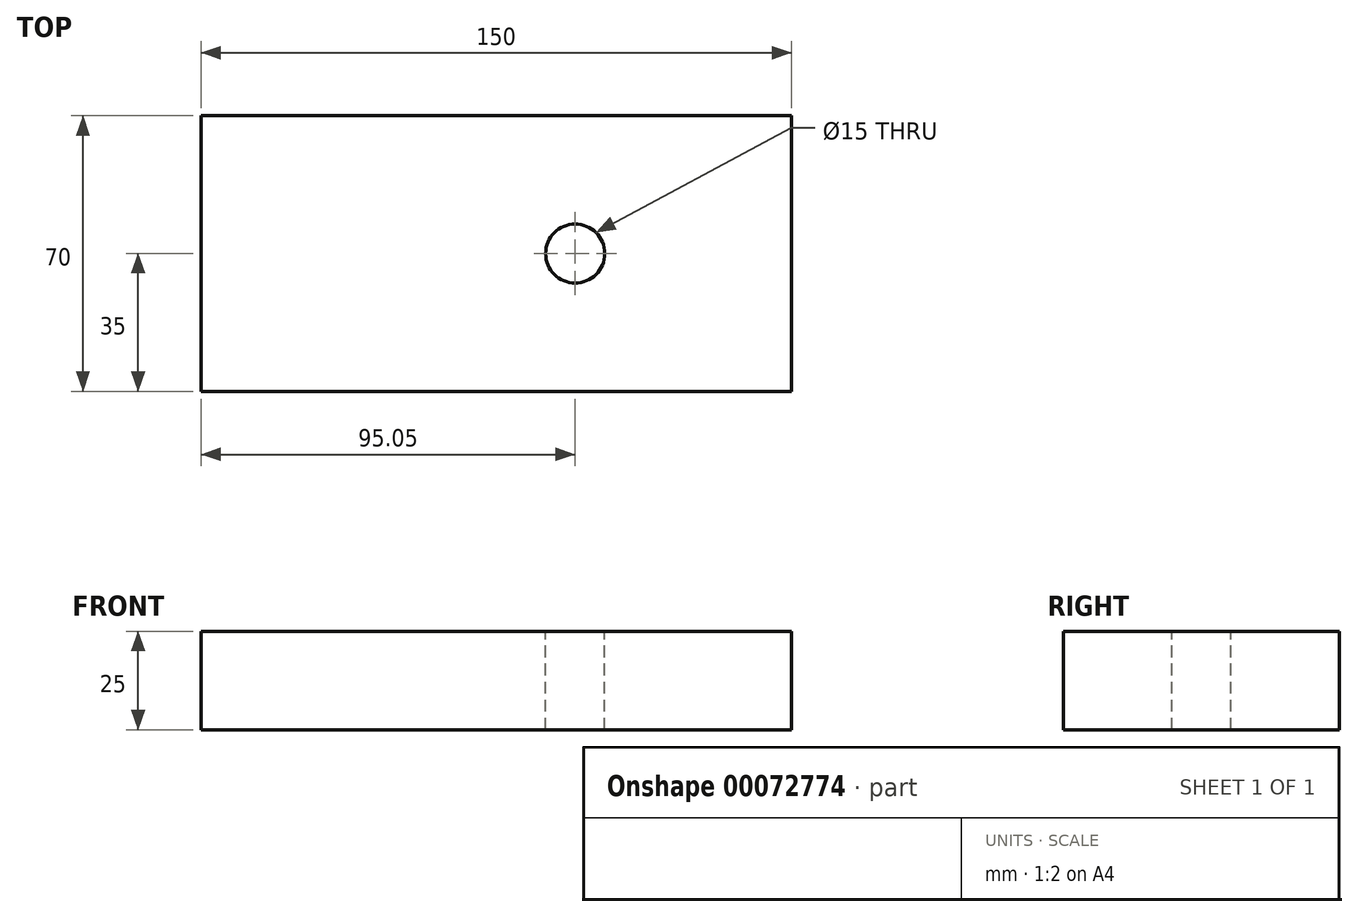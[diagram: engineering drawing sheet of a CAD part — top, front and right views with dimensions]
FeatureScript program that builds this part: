
annotation { "Feature Type Name" : "Feature", "Feature Type Description" : "" }
export const myFeature = defineFeature(function(context is Context, id is Id, definition is map)
    precondition{}
    {
        {
            var Q0;
            Q0=qCreatedBy(makeId("Top.planeOp"),FACE);
            var sketch = newSketch(context, id + "F0", { "sketchPlane" : qUnion([Q0])});
            skLineSegment(sketch, "E0.rect.bottom", {"start": v(75, 35) * mm, "end": v(-75, 35) * mm});
            skLineSegment(sketch, "E0.rect.top", {"start": v(75, -35) * mm, "end": v(-75, -35) * mm});
            skLineSegment(sketch, "E0.rect.left", {"start": v(75, 35) * mm, "end": v(75, -35) * mm});
            skLineSegment(sketch, "E0.rect.right", {"start": v(-75, 35) * mm, "end": v(-75, -35) * mm});
            skPoint(sketch, "E0.rect.middle", {"position": v(0, 0) * mm});
            skCircle(sketch, "E1", {"center": v(-20.05, 0) * mm, "radius": 7.5 * mm});
            skCircle(sketch, "E2.MirrorC", {"center": v(20.05, 0) * mm, "radius": 7.5 * mm});
            skSolve(sketch);
        }
        {
            var Q0;
            Q0=makeQuery(id+"F0.imprint","IMPRINT",FACE,{"disambiguationData":[TD([[makeQuery(id+"F0.imprint","IMPRINT",EDGE,{"derivedFrom":sQuery(id+"F0.wireOp",EDGE,"E0.rect.bottom")}),1.0]])]});
            var Q1;
            Q1=makeQuery(id+"F0.imprint","IMPRINT",FACE,{"disambiguationData":[TD([[makeQuery(id+"F0.imprint","IMPRINT",EDGE,{"derivedFrom":sQuery(id+"F0.wireOp",EDGE,"E2.MirrorC")}),-1.0]])]});
            var Q2;
            Q2=makeQuery(id+"F0.imprint","IMPRINT",FACE,{"disambiguationData":[TD([[makeQuery(id+"F0.imprint","IMPRINT",EDGE,{"derivedFrom":sQuery(id+"F0.wireOp",EDGE,"E1")}),1.0]])]});
            extrude(context, id + "F1", {"entities" : qUnion([Q0, Q1, Q2]), "oppositeDirection" : true, "depth" : 10 * mm});
        }
        {
            var Q0;
            Q0=makeQuery(id+"F0.imprint","IMPRINT",FACE,{"disambiguationData":[TD([[makeQuery(id+"F0.imprint","IMPRINT",EDGE,{"derivedFrom":sQuery(id+"F0.wireOp",EDGE,"E1")}),1.0]])]});
            var Q1;
            Q1=makeQuery(id+"F0.imprint","IMPRINT",FACE,{"disambiguationData":[TD([[makeQuery(id+"F0.imprint","IMPRINT",EDGE,{"derivedFrom":sQuery(id+"F0.wireOp",EDGE,"E2.MirrorC")}),-1.0]])]});
            extrude(context, id + "F2", {"entities" : qUnion([Q0, Q1]), "operationType" : NewBodyOperationType.ADD, "depth" : 15 * mm});
        }
    });
